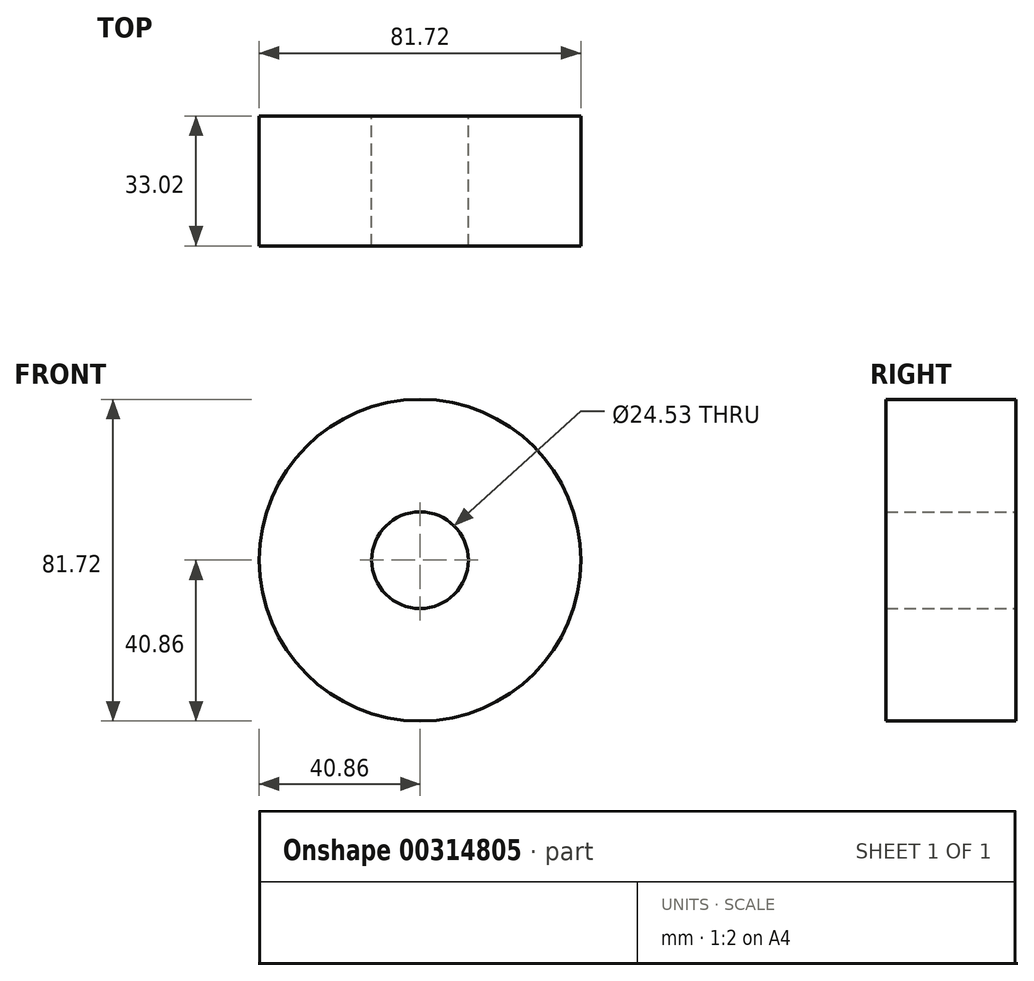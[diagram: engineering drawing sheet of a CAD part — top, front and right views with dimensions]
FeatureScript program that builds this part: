
annotation { "Feature Type Name" : "Feature", "Feature Type Description" : "" }
export const myFeature = defineFeature(function(context is Context, id is Id, definition is map)
    precondition{}
    {
        {
            var Q0;
            Q0=qCreatedBy(makeId("Front.planeOp"),FACE);
            var sketch = newSketch(context, id + "F0", { "sketchPlane" : qUnion([Q0])});
            skCircle(sketch, "E0", {"center": v(0, 0) * mm, "radius": 40.86 * mm});
            skCircle(sketch, "E1", {"center": v(0, 0) * mm, "radius": 28.96 * mm});
            skCircle(sketch, "E2", {"center": v(0, 0) * mm, "radius": 12.27 * mm});
            skSolve(sketch);
        }
        {
            var Q0;
            Q0=makeQuery(id+"F0.imprint","IMPRINT",FACE,{"disambiguationData":[TD([[makeQuery(id+"F0.imprint","IMPRINT",EDGE,{"derivedFrom":sQuery(id+"F0.wireOp",EDGE,"E1")}),1.0]])]});
            var sketch = newSketch(context, id + "F1", { "sketchPlane" : qUnion([Q0])});
            skLineSegment(sketch, "E3", {"start": v(11.21, 26.35) * mm, "end": v(8.54, 7.59) * mm});
            skLineSegment(sketch, "E4", {"start": v(-2.02, 28.05) * mm, "end": v(-4.44, 11) * mm});
            skSolve(sketch);
        }
        {
            var Q0;
            Q0=makeQuery(id+"F1.imprint","IMPRINT",FACE,{"disambiguationData":[TD([[makeQuery(id+"F1.imprint","IMPRINT",EDGE,{"derivedFrom":makeQuery(id+"F0.imprint","IMPRINT",EDGE,{"derivedFrom":sQuery(id+"F0.wireOp",EDGE,"E1")})}),1.0]])]});
            var Q1;
            Q1=makeQuery(id+"F0.imprint","IMPRINT",FACE,{"disambiguationData":[TD([[makeQuery(id+"F0.imprint","IMPRINT",EDGE,{"derivedFrom":sQuery(id+"F0.wireOp",EDGE,"E1")}),1.0]])]});
            var Q2;
            Q2=makeQuery(id+"F0.imprint","IMPRINT",FACE,{"disambiguationData":[TD([[makeQuery(id+"F0.imprint","IMPRINT",EDGE,{"derivedFrom":sQuery(id+"F0.wireOp",EDGE,"E0")}),1.0]])]});
            extrude(context, id + "F2", {"entities" : qUnion([Q0, Q1, Q2]), "depth" : 7.62 * mm});
        }
        {
            var Q0;
            Q0=makeQuery(id+"F2.opExtrude","CAP_FACE",FACE,{"disambiguationData":[OSD([sQuery(id+"F0.wireOp",EDGE,"E0"),sQuery(id+"F0.wireOp",EDGE,"E2")])],"isStart":false});
            extrude(context, id + "F3", {"entities" : qUnion([Q0]), "operationType" : NewBodyOperationType.ADD, "depth" : 25.4 * mm});
        }
    });
